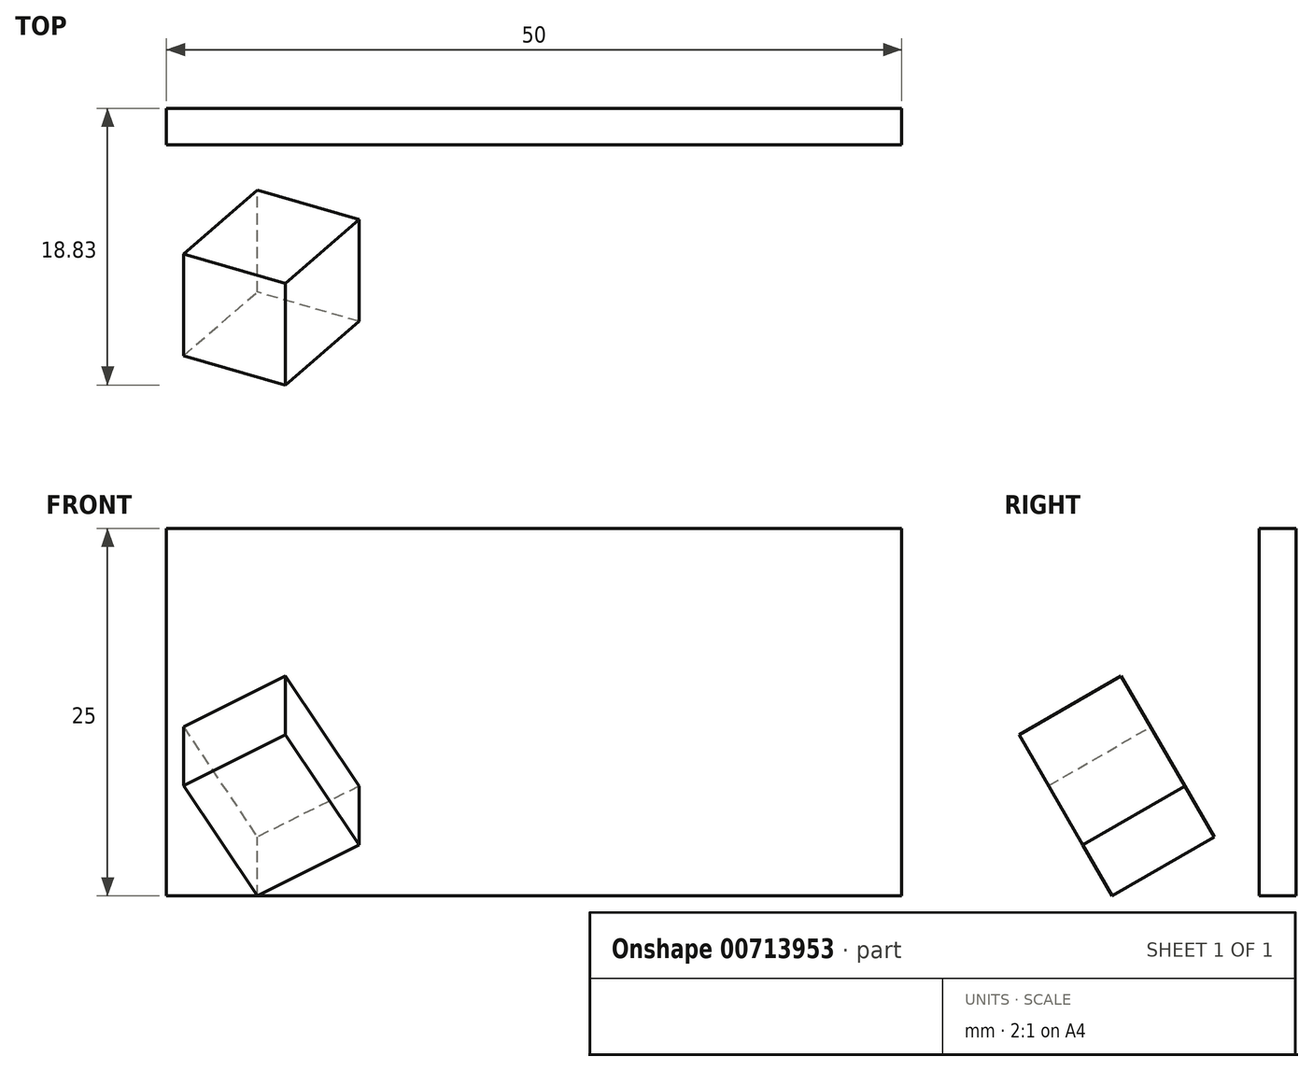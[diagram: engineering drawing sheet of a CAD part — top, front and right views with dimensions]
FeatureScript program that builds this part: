
annotation { "Feature Type Name" : "Feature", "Feature Type Description" : "" }
export const myFeature = defineFeature(function(context is Context, id is Id, definition is map)
    precondition{}
    {
        {
            var Q0;
            Q0=qCreatedBy(makeId("Top.planeOp"),FACE);
            var sketch = newSketch(context, id + "F0", { "sketchPlane" : qUnion([Q0])});
            skLineSegment(sketch, "E0.bottom", {"start": v(-25.19, 0) * mm, "end": v(24.81, 0) * mm});
            skLineSegment(sketch, "E0.top", {"start": v(-25.19, 2.5) * mm, "end": v(24.81, 2.5) * mm});
            skLineSegment(sketch, "E0.left", {"start": v(-25.19, 0) * mm, "end": v(-25.19, 2.5) * mm});
            skLineSegment(sketch, "E0.right", {"start": v(24.81, 0) * mm, "end": v(24.81, 2.5) * mm});
            skLineSegment(sketch, "E1.bottom", {"start": v(-16.51, 0) * mm, "end": v(-7.66, 0) * mm});
            skSolve(sketch);
        }
        {
            var Q0;
            Q0=makeQuery(id+"F0.imprint","IMPRINT",FACE,{"disambiguationData":[TD([[makeQuery(id+"F0.imprint","IMPRINT",EDGE,{"derivedFrom":sQuery(id+"F0.wireOp",EDGE,"E0.top")}),-1.0]])]});
            extrude(context, id + "F1", {"entities" : qUnion([Q0]), "depth" : 25 * mm, "offsetDistance" : 25 * mm});
        }
        {
            var Q0;
            Q0=qCreatedBy(makeId("Top.planeOp"),FACE);
            var sketch = newSketch(context, id + "F2", { "sketchPlane" : qUnion([Q0])});
            skLineSegment(sketch, "E2.bottom", {"start": v(-11.02, -10) * mm, "end": v(-19.02, -10) * mm});
            skLineSegment(sketch, "E2.top", {"start": v(-11.02, -2) * mm, "end": v(-19.02, -2) * mm});
            skLineSegment(sketch, "E2.left", {"start": v(-11.02, -10) * mm, "end": v(-11.02, -2) * mm});
            skLineSegment(sketch, "E2.right", {"start": v(-19.02, -10) * mm, "end": v(-19.02, -2) * mm});
            skSolve(sketch);
        }
        {
            var Q0;
            Q0 = qSketchRegion(id + "F2", true);
            extrude(context, id + "F3", {"entities" : qUnion([Q0]), "depth" : 10 * mm, "offsetDistance" : 25 * mm});
        }
        {
            var Q0;
            Q0=makeQuery(id+"F3.opExtrude","SWEPT_BODY",BODY,{"disambiguationData":[OSD([sQuery(id+"F2.wireOp",EDGE,"E2.bottom"),sQuery(id+"F2.wireOp",EDGE,"E2.top"),sQuery(id+"F2.wireOp",EDGE,"E2.left"),sQuery(id+"F2.wireOp",EDGE,"E2.right")])]});
            var Q1;
            Q1=makeQuery(id+"F3.opExtrude","CAP_EDGE",EDGE,{"disambiguationData":[OSD([sQuery(id+"F2.wireOp",EDGE,"E2.bottom")])],"isStart":true});
            transform(context, id + "F4", {"entities" : qUnion([Q0]), "transformType" : TransformType.ROTATION, "transformAxis" : qUnion([Q1]), "angle" : 30 * degree, "oppositeDirection" : true, "makeCopy" : false});
        }
        {
            var Q0;
            Q0=makeQuery(id+"F3.opExtrude","SWEPT_BODY",BODY,{"disambiguationData":[OSD([sQuery(id+"F2.wireOp",EDGE,"E2.bottom"),sQuery(id+"F2.wireOp",EDGE,"E2.top"),sQuery(id+"F2.wireOp",EDGE,"E2.left"),sQuery(id+"F2.wireOp",EDGE,"E2.right")])]});
            var Q1;
            Q1=makeQuery(id+"F3.opExtrude","CAP_EDGE",EDGE,{"disambiguationData":[OSD([sQuery(id+"F2.wireOp",EDGE,"E2.right")])],"isStart":true});
            transform(context, id + "F5", {"entities" : qUnion([Q0]), "transformType" : TransformType.ROTATION, "transformAxis" : qUnion([Q1]), "angle" : 30 * degree, "oppositeDirection" : true, "makeCopy" : false});
        }
    });
